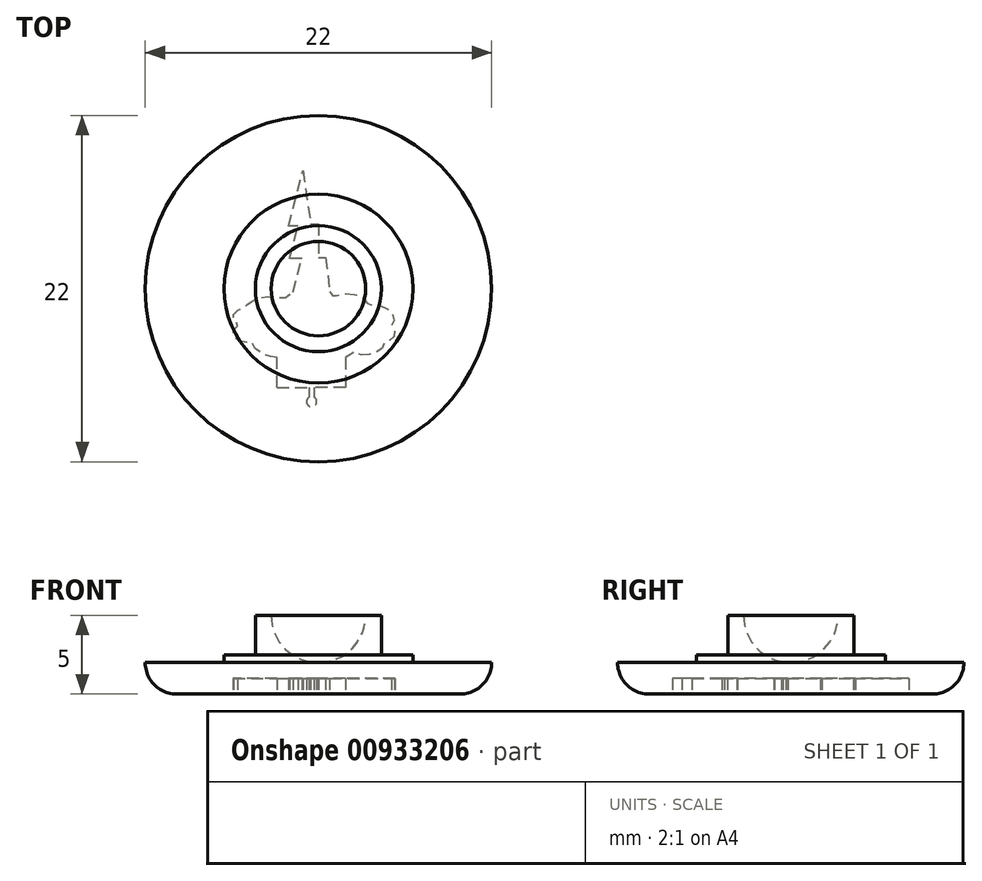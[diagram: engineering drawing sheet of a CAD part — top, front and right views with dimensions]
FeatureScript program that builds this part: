
annotation { "Feature Type Name" : "Feature", "Feature Type Description" : "" }
export const myFeature = defineFeature(function(context is Context, id is Id, definition is map)
    precondition{}
    {
        {
            var Q0;
            Q0=qCreatedBy(makeId("Top.planeOp"),FACE);
            var sketch = newSketch(context, id + "F0", { "sketchPlane" : qUnion([Q0])});
            skCircle(sketch, "E0", {"center": v(0, 0) * mm, "radius": 11 * mm});
            skSolve(sketch);
        }
        {
            var Q0;
            Q0=makeQuery(id+"F0.imprint","IMPRINT",FACE,{"disambiguationData":[TD([[makeQuery(id+"F0.imprint","IMPRINT",EDGE,{"derivedFrom":sQuery(id+"F0.wireOp",EDGE,"E0")}),1.0]])]});
            extrude(context, id + "F1", {"entities" : qUnion([Q0]), "depth" : 2 * mm, "offsetDistance" : 25 * mm});
        }
        {
            var Q0;
            Q0=makeQuery(id+"F1.opExtrude","CAP_FACE",FACE,{"disambiguationData":[OSD([sQuery(id+"F0.wireOp",EDGE,"E0")])],"isStart":false});
            var sketch = newSketch(context, id + "F2", { "sketchPlane" : qUnion([Q0])});
            skCircle(sketch, "E1", {"center": v(0, 0) * mm, "radius": 4 * mm});
            skSolve(sketch);
        }
        {
            var Q0;
            Q0=makeQuery(id+"F2.imprint","IMPRINT",FACE,{"disambiguationData":[TD([[makeQuery(id+"F2.imprint","IMPRINT",EDGE,{"derivedFrom":sQuery(id+"F2.wireOp",EDGE,"E1")}),1.0]])]});
            extrude(context, id + "F3", {"entities" : qUnion([Q0]), "operationType" : NewBodyOperationType.ADD, "depth" : 3 * mm, "offsetDistance" : 25 * mm});
        }
        {
            var Q0;
            Q0=makeQuery(id+"F1.opExtrude","CAP_EDGE",EDGE,{"disambiguationData":[OSD([sQuery(id+"F0.wireOp",EDGE,"E0")])],"isStart":true});
            fillet(context, id + "F4", {"entities" : qUnion([Q0]), "radius" : 2 * mm, "tangentPropagation" : true, "allowEdgeOverflow" : false});
        }
        {
            var Q0;
            Q0=makeQuery(id+"F1.opExtrude","CAP_FACE",FACE,{"disambiguationData":[OSD([sQuery(id+"F0.wireOp",EDGE,"E0")])],"isStart":true});
            var sketch = newSketch(context, id + "F5", { "sketchPlane" : qUnion([Q0])});
            skLineSegment(sketch, "E2", {"start": v(-9, 0) * mm, "end": v(9, 0) * mm, "construction": true});
            skPoint(sketch, "E3", {"position": v(7.24, 0) * mm});
            skLineSegment(sketch, "E4", {"start": v(-0.98, -7.5) * mm, "end": v(-0.48, -4.12) * mm});
            skLineSegment(sketch, "E5", {"start": v(-0.48, -4.12) * mm, "end": v(0, -4.12) * mm});
            skLineSegment(sketch, "E6", {"start": v(0, -4.12) * mm, "end": v(0, -1.97) * mm});
            skLineSegment(sketch, "E7", {"start": v(0, -1.97) * mm, "end": v(0.46, -1.97) * mm});
            skLineSegment(sketch, "E8", {"start": v(0.46, -1.97) * mm, "end": v(0.72, 0.18) * mm});
            skFitSpline(sketch, "E9", {"points": [v(0.72, 0.18) * mm, v(0.85, 0.38) * mm, v(0.96, 0.5) * mm, v(1.36, 0.36) * mm, v(2.27, 0.36) * mm, v(2.9, 0.64) * mm, v(3.2, 1.04) * mm, v(3.68, 1.05) * mm, v(4.3, 1.25) * mm, v(4.7, 1.62) * mm, v(4.8, 2.04) * mm, v(4.65, 2.35) * mm, v(4.81, 2.59) * mm, v(4.84, 2.96) * mm, v(4.47, 3.34) * mm, v(4.18, 3.43) * mm, v(4.1, 3.68) * mm, v(3.78, 4) * mm, v(3.26, 4.18) * mm, v(2.71, 4.2) * mm, v(2.2, 4.02) * mm, v(2.04, 4.2) * mm, v(1.72, 4.37) * mm], "startDerivative": vector(4.7, 4.45) * mm, "endDerivative": vector(-9.17, 2.55) * mm});
            skLineSegment(sketch, "E10", {"start": v(1.72, 4.37) * mm, "end": v(1.72, 6.28) * mm});
            skLineSegment(sketch, "E11", {"start": v(-2.62, 6.27) * mm, "end": v(-2.62, 4.37) * mm});
            skFitSpline(sketch, "E12", {"points": [v(-2.62, 4.37) * mm, v(-3.14, 4.3) * mm, v(-3.98, 3.85) * mm, v(-4.2, 3.42) * mm, v(-4.45, 3.42) * mm, v(-4.86, 3.36) * mm, v(-5.21, 3.18) * mm, v(-5.4, 2.94) * mm, v(-5.39, 2.64) * mm, v(-5.15, 2.38) * mm, v(-5.16, 2.21) * mm, v(-5.3, 2.06) * mm, v(-5.38, 1.92) * mm, v(-5.38, 1.63) * mm, v(-5.04, 1.33) * mm, v(-4.67, 1.22) * mm, v(-4.55, 1.05) * mm, v(-4.16, 0.78) * mm, v(-3.35, 0.5) * mm, v(-2.23, 0.58) * mm, v(-2.02, 0.55) * mm, v(-1.95, 0.44) * mm, v(-1.62, 0.22) * mm], "startDerivative": vector(-8.72, -0.22) * mm, "endDerivative": vector(8.66, -4.85) * mm});
            skLineSegment(sketch, "E13", {"start": v(-1.62, 0.22) * mm, "end": v(-1.05, -1.9) * mm});
            skLineSegment(sketch, "E14", {"start": v(-1.05, -1.9) * mm, "end": v(-1.82, -1.9) * mm});
            skLineSegment(sketch, "E15", {"start": v(-1.82, -1.9) * mm, "end": v(-1.29, -3.98) * mm});
            skLineSegment(sketch, "E16", {"start": v(-1.29, -3.98) * mm, "end": v(-1.9, -3.98) * mm});
            skLineSegment(sketch, "E17", {"start": v(-1.9, -3.98) * mm, "end": v(-0.98, -7.5) * mm});
            skLineSegment(sketch, "E18", {"start": v(-2.62, 6.27) * mm, "end": v(-0.58, 6.27) * mm});
            skLineSegment(sketch, "E19", {"start": v(-0.58, 6.27) * mm, "end": v(-0.58, 6.9) * mm});
            skLineSegment(sketch, "E20", {"start": v(1.72, 6.28) * mm, "end": v(-0.28, 6.28) * mm});
            skLineSegment(sketch, "E21", {"start": v(-0.28, 6.28) * mm, "end": v(-0.28, 6.9) * mm});
            skArc(sketch, "E22", {"start": v(-0.28, 6.9) * mm, "mid": v(-0.43, 7.5) * mm, "end": v(-0.58, 6.9) * mm});
            skSolve(sketch);
        }
        {
            var Q0;
            Q0=makeQuery(id+"F5.imprint","IMPRINT",FACE,{"disambiguationData":[TD([[makeQuery(id+"F5.imprint","IMPRINT",EDGE,{"derivedFrom":sQuery(id+"F5.wireOp",EDGE,"E4")}),1.0]])]});
            extrude(context, id + "F6", {"entities" : qUnion([Q0]), "surfaceOperationType" : NewSurfaceOperationType.ADD, "oppositeDirection" : true, "depth" : 1 * mm, "offsetDistance" : 25 * mm});
        }
        {
            var Q0;
            Q0=makeQuery(id+"F6.opExtrude","SWEPT_BODY",BODY,{"disambiguationData":[OSD([sQuery(id+"F5.wireOp",EDGE,"E4"),sQuery(id+"F5.wireOp",EDGE,"E5"),sQuery(id+"F5.wireOp",EDGE,"E6"),sQuery(id+"F5.wireOp",EDGE,"E7"),sQuery(id+"F5.wireOp",EDGE,"E8"),sQuery(id+"F5.wireOp",EDGE,"E9"),sQuery(id+"F5.wireOp",EDGE,"E10"),sQuery(id+"F5.wireOp",EDGE,"E11"),sQuery(id+"F5.wireOp",EDGE,"E12"),sQuery(id+"F5.wireOp",EDGE,"E13"),sQuery(id+"F5.wireOp",EDGE,"E14"),sQuery(id+"F5.wireOp",EDGE,"E15"),sQuery(id+"F5.wireOp",EDGE,"E16"),sQuery(id+"F5.wireOp",EDGE,"E17"),sQuery(id+"F5.wireOp",EDGE,"E18"),sQuery(id+"F5.wireOp",EDGE,"E19"),sQuery(id+"F5.wireOp",EDGE,"E20"),sQuery(id+"F5.wireOp",EDGE,"E21"),sQuery(id+"F5.wireOp",EDGE,"E22")])]});
            var Q1;
            Q1=makeQuery(id+"F1.opExtrude","SWEPT_BODY",BODY,{"disambiguationData":[OSD([sQuery(id+"F0.wireOp",EDGE,"E0")])]});
            booleanBodies(context, id + "F7", {"operationType" : BooleanOperationType.SUBTRACTION, "tools" : qUnion([Q0]), "targets" : qUnion([Q1]), "keepTools" : true});
        }
        {
            var Q0;
            Q0=makeQuery(id+"F3.opExtrude","CAP_FACE",FACE,{"disambiguationData":[OSD([sQuery(id+"F2.wireOp",EDGE,"E1")])],"isStart":false});
            var sketch = newSketch(context, id + "F8", { "sketchPlane" : qUnion([Q0])});
            skCircle(sketch, "E23", {"center": v(0, 0) * mm, "radius": 3 * mm});
            skSolve(sketch);
        }
        {
            var Q0;
            Q0=makeQuery(id+"F8.imprint","IMPRINT",FACE,{"disambiguationData":[TD([[makeQuery(id+"F8.imprint","IMPRINT",EDGE,{"derivedFrom":sQuery(id+"F8.wireOp",EDGE,"E23")}),1.0]])]});
            var Q1;
            Q1=makeQuery(id+"F1.opExtrude","CAP_FACE",FACE,{"disambiguationData":[OSD([sQuery(id+"F0.wireOp",EDGE,"E0")])],"isStart":false});
            extrude(context, id + "F9", {"entities" : qUnion([Q0]), "operationType" : NewBodyOperationType.REMOVE, "endBound" : BoundingType.UP_TO_SURFACE, "oppositeDirection" : true, "depth" : 25 * mm, "endBoundEntityFace" : qUnion([Q1]), "offsetDistance" : 25 * mm});
        }
        {
            var Q0;
            Q0=makeQuery(id+"F9.boolean.opBoolean","COPY",EDGE,{"derivedFrom":makeQuery(id+"F9.opExtrude","CAP_EDGE",EDGE,{"disambiguationData":[OSD([sQuery(id+"F8.wireOp",EDGE,"E23")])],"isStart":false})});
            fillet(context, id + "F10", {"entities" : qUnion([Q0]), "radius" : 3 * mm, "tangentPropagation" : true, "allowEdgeOverflow" : false});
        }
        {
            var Q0;
            Q0=makeQuery(id+"F1.opExtrude","CAP_FACE",FACE,{"disambiguationData":[OSD([sQuery(id+"F0.wireOp",EDGE,"E0")])],"isStart":false});
            var sketch = newSketch(context, id + "F11", { "sketchPlane" : qUnion([Q0])});
            skCircle(sketch, "E24", {"center": v(0, 0) * mm, "radius": 6 * mm});
            skSolve(sketch);
        }
        {
            var Q0;
            Q0=makeQuery(id+"F11.imprint","IMPRINT",FACE,{"disambiguationData":[TD([[makeQuery(id+"F11.imprint","IMPRINT",EDGE,{"derivedFrom":sQuery(id+"F11.wireOp",EDGE,"E24")}),1.0]])]});
            extrude(context, id + "F12", {"entities" : qUnion([Q0]), "operationType" : NewBodyOperationType.ADD, "depth" : 0.5 * mm, "offsetDistance" : 25 * mm});
        }
    });
